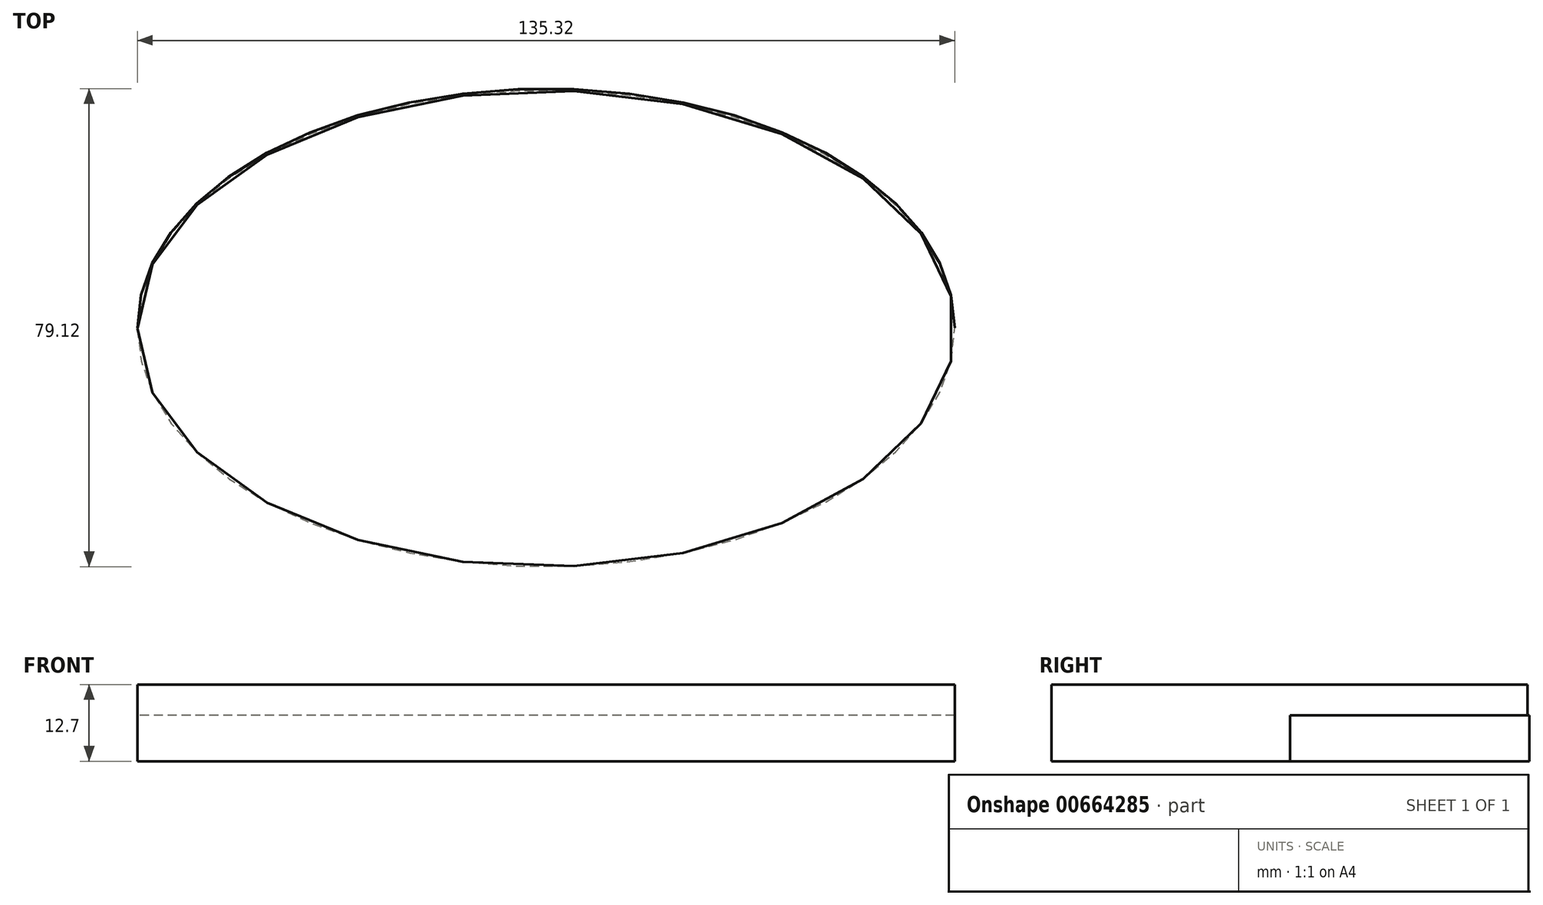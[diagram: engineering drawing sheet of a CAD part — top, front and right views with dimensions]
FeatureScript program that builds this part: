
annotation { "Feature Type Name" : "Feature", "Feature Type Description" : "" }
export const myFeature = defineFeature(function(context is Context, id is Id, definition is map)
    precondition{}
    {
        {
            var Q0;
            Q0=qCreatedBy(makeId("Top.planeOp"),FACE);
            var sketch = newSketch(context, id + "F0", { "sketchPlane" : qUnion([Q0])});
            skFitSpline(sketch, "E0", {"points": [v(0, -23.42) * mm, v(-13.86, -7.28) * mm, v(-19.95, -14.69) * mm], "startDerivative": vector(-25.56, 40.56) * mm, "endDerivative": vector(-13.54, -27.56) * mm});
            skFitSpline(sketch, "E1", {"points": [v(-19.95, -14.69) * mm, v(-33.17, -4.1) * mm, v(-40.05, -8.34) * mm, v(-36.88, -19.19) * mm], "startDerivative": vector(-33.24, 38.26) * mm, "endDerivative": vector(19.14, -35.96) * mm});
            skFitSpline(sketch, "E2", {"points": [v(-36.88, -19.19) * mm, v(-57.25, -4.1) * mm, v(-57.78, 20.76) * mm, v(-23.12, 41.4) * mm], "startDerivative": vector(-78.07, 38.72) * mm, "endDerivative": vector(111.58, 42.37) * mm});
            skFitSpline(sketch, "E3", {"points": [v(-23.12, 41.4) * mm, v(-26.82, 21.3) * mm, v(-18.13, 15.47) * mm, v(-9.1, 41.4) * mm], "startDerivative": vector(-25.2, -63.16) * mm, "endDerivative": vector(15.32, 90.23) * mm});
            skLineSegment(sketch, "E4", {"start": v(-9.1, 41.4) * mm, "end": v(-5.13, 36.64) * mm});
            skLineSegment(sketch, "E5", {"start": v(-5.13, 36.64) * mm, "end": v(0, 36.64) * mm});
            skLineSegment(sketch, "E6", {"start": v(0, 36.64) * mm, "end": v(0, -23.42) * mm, "construction": true});
            skFitSpline(sketch, "E7.MirrorCS", {"points": [v(0, -23.42) * mm, v(13.86, -7.28) * mm, v(19.95, -14.69) * mm], "startDerivative": vector(25.56, 40.56) * mm, "endDerivative": vector(13.54, -27.56) * mm});
            skFitSpline(sketch, "E8.MirrorCS", {"points": [v(19.95, -14.69) * mm, v(33.17, -4.1) * mm, v(40.05, -8.34) * mm, v(36.88, -19.19) * mm], "startDerivative": vector(33.24, 38.26) * mm, "endDerivative": vector(-19.14, -35.96) * mm});
            skLineSegment(sketch, "E9.MirrorCS", {"start": v(9.1, 41.4) * mm, "end": v(5.13, 36.64) * mm});
            skLineSegment(sketch, "E10.MirrorCS", {"start": v(5.13, 36.64) * mm, "end": v(0, 36.64) * mm});
            skFitSpline(sketch, "E11.MirrorCS", {"points": [v(23.12, 41.4) * mm, v(26.82, 21.3) * mm, v(18.13, 15.47) * mm, v(9.1, 41.4) * mm], "startDerivative": vector(25.2, -63.16) * mm, "endDerivative": vector(-15.32, 90.23) * mm});
            skFitSpline(sketch, "E12.MirrorCS", {"points": [v(36.88, -19.19) * mm, v(57.25, -4.1) * mm, v(57.78, 20.76) * mm, v(23.12, 41.4) * mm], "startDerivative": vector(78.07, 38.72) * mm, "endDerivative": vector(-111.58, 42.37) * mm});
            skSolve(sketch);
        }
        {
            var Q0;
            Q0 = qSketchRegion(id + "F0", true);
            extrude(context, id + "F1", {"entities" : qUnion([Q0]), "depth" : 12.7 * mm, "offsetDistance" : 25.4 * mm});
        }
        {
            var Q0;
            Q0=qCreatedBy(makeId("Top.planeOp"),FACE);
            var sketch = newSketch(context, id + "F2", { "sketchPlane" : qUnion([Q0])});
            skEllipse(sketch, "E13", {"center": v(0, 8.84) * mm, "majorRadius": 67.66 * mm, "minorRadius": 39.45 * mm, "majorAxis": v(-1, 0)});
            skSolve(sketch);
        }
        {
            var Q0;
            Q0 = qSketchRegion(id + "F2", true);
            extrude(context, id + "F3", {"entities" : qUnion([Q0]), "operationType" : NewBodyOperationType.ADD, "depth" : 7.62 * mm, "offsetDistance" : 25.4 * mm});
        }
        {
            var Q0;
            Q0=qCreatedBy(makeId("Top.planeOp"),FACE);
            var sketch = newSketch(context, id + "F4", { "sketchPlane" : qUnion([Q0])});
            skEllipse(sketch, "E14", {"center": v(0, 8.57) * mm, "majorRadius": 67.66 * mm, "minorRadius": 39.4 * mm, "majorAxis": v(-1, 0)});
            skFitSpline(sketch, "E15.0", {"points": [v(-65.07, 10.3) * mm, v(-65.15, 8.57) * mm, v(-65.07, 6.83) * mm, v(-64.78, 4.52) * mm, v(-64.05, 1.66) * mm, v(-62.59, -1.73) * mm, v(-60.54, -5.05) * mm, v(-57.92, -8.29) * mm, v(-54.72, -11.4) * mm, v(-51.59, -13.87) * mm, v(-48.8, -15.75) * mm, v(-46.59, -17.1) * mm, v(-44.25, -18.4) * mm, v(-41, -20.04) * mm, v(-36.68, -21.9) * mm, v(-31.16, -23.82) * mm, v(-25.34, -25.42) * mm, v(-19.27, -26.68) * mm, v(-13, -27.6) * mm, v(-7.63, -28.07) * mm, v(-3.29, -28.26) * mm, v(0, -28.3) * mm, v(3.29, -28.26) * mm, v(7.63, -28.07) * mm, v(13, -27.6) * mm, v(19.27, -26.68) * mm, v(25.34, -25.42) * mm, v(31.16, -23.82) * mm, v(36.68, -21.9) * mm, v(41, -20.04) * mm, v(44.25, -18.4) * mm, v(46.59, -17.1) * mm, v(48.8, -15.75) * mm, v(51.59, -13.87) * mm, v(54.72, -11.4) * mm, v(57.92, -8.29) * mm, v(60.54, -5.05) * mm, v(62.59, -1.73) * mm, v(64.05, 1.66) * mm, v(64.78, 4.52) * mm, v(65.07, 6.83) * mm, v(65.15, 8.57) * mm, v(65.07, 10.3) * mm, v(64.78, 12.61) * mm, v(64.05, 15.47) * mm, v(62.59, 18.86) * mm, v(60.54, 22.19) * mm, v(57.92, 25.42) * mm, v(54.72, 28.54) * mm, v(51.59, 31) * mm, v(48.8, 32.88) * mm, v(46.59, 34.24) * mm, v(44.25, 35.54) * mm, v(41, 37.17) * mm, v(36.68, 39.03) * mm, v(31.16, 40.95) * mm, v(25.34, 42.55) * mm, v(19.27, 43.82) * mm, v(13, 44.74) * mm, v(7.63, 45.2) * mm, v(3.29, 45.4) * mm, v(0, 45.44) * mm, v(-3.29, 45.4) * mm, v(-7.63, 45.2) * mm, v(-13, 44.74) * mm, v(-19.27, 43.82) * mm, v(-25.34, 42.55) * mm, v(-31.16, 40.95) * mm, v(-36.68, 39.03) * mm, v(-41, 37.17) * mm, v(-44.25, 35.54) * mm, v(-46.59, 34.24) * mm, v(-48.8, 32.88) * mm, v(-51.59, 31) * mm, v(-54.72, 28.54) * mm, v(-57.92, 25.42) * mm, v(-60.54, 22.19) * mm, v(-62.59, 18.86) * mm, v(-64.05, 15.47) * mm, v(-64.78, 12.61) * mm, v(-65.07, 10.3) * mm, v(-65.15, 8.57) * mm, v(-65.07, 6.83) * mm, v(-65.07, 10.3) * mm]});
            skSolve(sketch);
        }
        {
            var Q0;
            Q0 = qSketchRegion(id + "F4", true);
            extrude(context, id + "F5", {"entities" : qUnion([Q0]), "operationType" : NewBodyOperationType.ADD, "depth" : 12.7 * mm, "offsetDistance" : 25.4 * mm});
        }
    });
